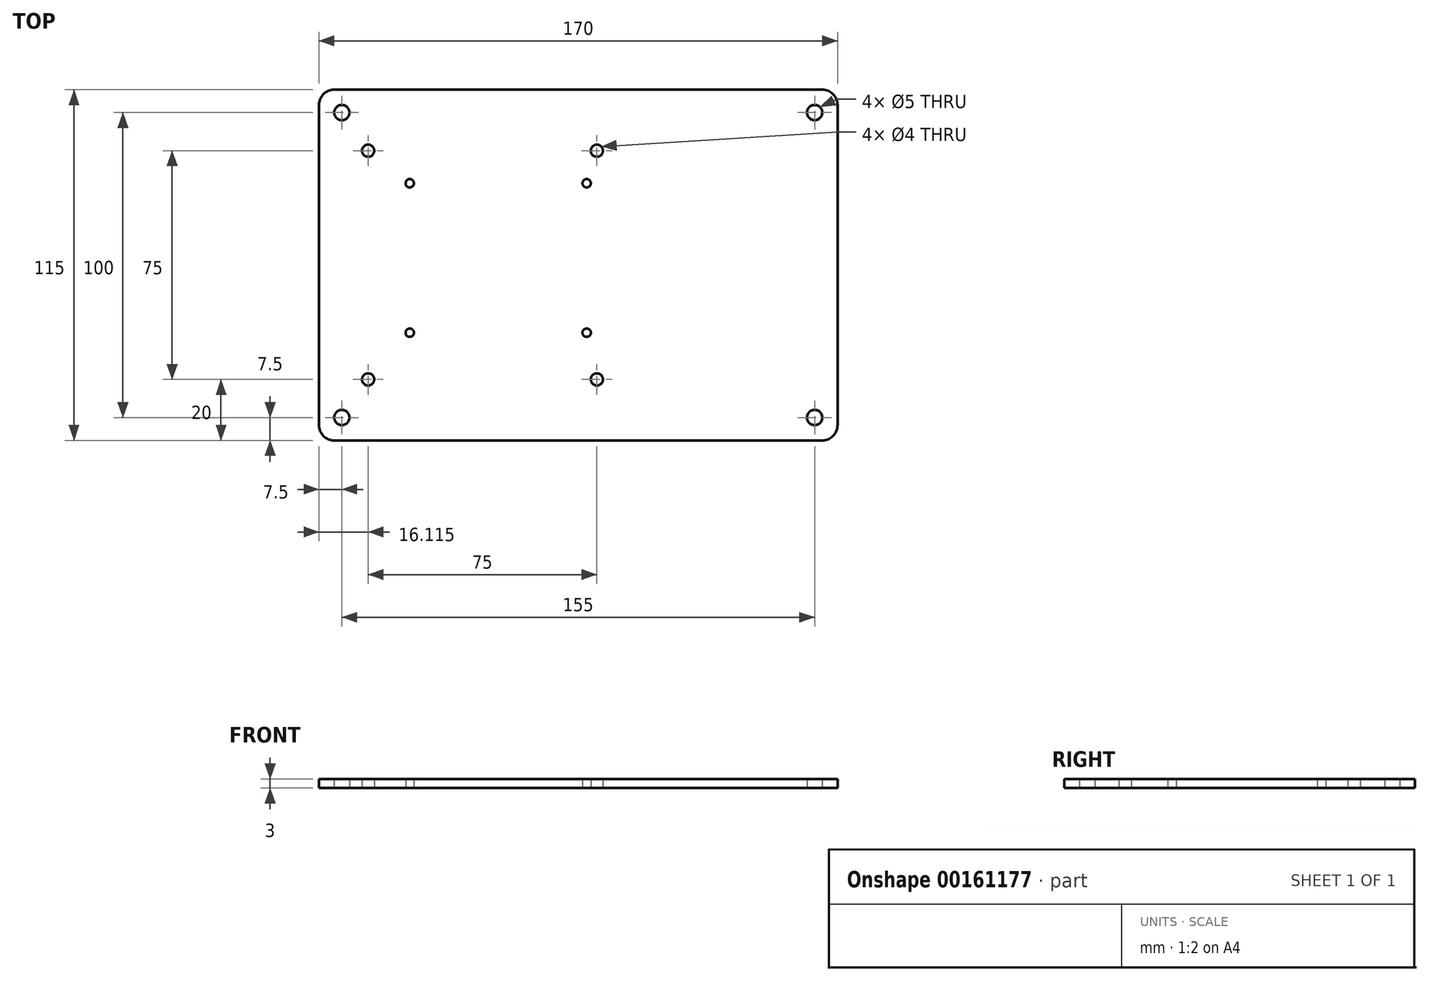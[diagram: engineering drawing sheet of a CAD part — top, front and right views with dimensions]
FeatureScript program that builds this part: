
annotation { "Feature Type Name" : "Feature", "Feature Type Description" : "" }
export const myFeature = defineFeature(function(context is Context, id is Id, definition is map)
    precondition{}
    {
        {
            var Q0;
            Q0=qCreatedBy(makeId("Top.planeOp"),FACE);
            var sketch = newSketch(context, id + "F0", { "sketchPlane" : qUnion([Q0])});
            skLineSegment(sketch, "E0.bottom", {"start": v(-85, 57.5) * mm, "end": v(85, 57.5) * mm});
            skLineSegment(sketch, "E0.top", {"start": v(-85, -57.5) * mm, "end": v(85, -57.5) * mm});
            skLineSegment(sketch, "E0.left", {"start": v(-85, 57.5) * mm, "end": v(-85, -57.5) * mm});
            skLineSegment(sketch, "E0.right", {"start": v(85, 57.5) * mm, "end": v(85, -57.5) * mm});
            skCircle(sketch, "E1", {"center": v(-77.5, 50) * mm, "radius": 2.5 * mm});
            skCircle(sketch, "E2.MirrorC", {"center": v(77.5, 50) * mm, "radius": 2.5 * mm});
            skCircle(sketch, "E3.MirrorC", {"center": v(-77.5, -50) * mm, "radius": 2.5 * mm});
            skCircle(sketch, "E4.MirrorC", {"center": v(77.5, -50) * mm, "radius": 2.5 * mm});
            skCircle(sketch, "E5", {"center": v(-55.23, 26.82) * mm, "radius": 1.38 * mm});
            skCircle(sketch, "E6", {"center": v(2.77, 26.82) * mm, "radius": 1.38 * mm});
            skCircle(sketch, "E7", {"center": v(-55.23, -22.18) * mm, "radius": 1.38 * mm});
            skCircle(sketch, "E8", {"center": v(2.77, -22.18) * mm, "radius": 1.38 * mm});
            skCircle(sketch, "E9", {"center": v(-68.89, 37.5) * mm, "radius": 2 * mm});
            skCircle(sketch, "E10", {"center": v(6.11, 37.5) * mm, "radius": 2 * mm});
            skCircle(sketch, "E11", {"center": v(-68.89, -37.5) * mm, "radius": 2 * mm});
            skCircle(sketch, "E12", {"center": v(6.11, -37.5) * mm, "radius": 2 * mm});
            skSolve(sketch);
        }
        {
            var Q0;
            Q0 = qSketchRegion(id + "F0", true);
            extrude(context, id + "F1", {"entities" : qUnion([Q0]), "depth" : 3 * mm});
        }
        {
            var Q0;
            Q0=makeQuery(id+"F1.opExtrude","SWEPT_EDGE",EDGE,{"disambiguationData":[OSD([sQuery(id+"F0.wireOp",EDGE,"E0.bottom"),sQuery(id+"F0.wireOp",EDGE,"E0.left")])]});
            var Q1;
            Q1=makeQuery(id+"F1.opExtrude","SWEPT_EDGE",EDGE,{"disambiguationData":[OSD([sQuery(id+"F0.wireOp",EDGE,"E0.top"),sQuery(id+"F0.wireOp",EDGE,"E0.right")])]});
            var Q2;
            Q2=makeQuery(id+"F1.opExtrude","SWEPT_EDGE",EDGE,{"disambiguationData":[OSD([sQuery(id+"F0.wireOp",EDGE,"E0.bottom"),sQuery(id+"F0.wireOp",EDGE,"E0.right")])]});
            var Q3;
            Q3=makeQuery(id+"F1.opExtrude","SWEPT_EDGE",EDGE,{"disambiguationData":[OSD([sQuery(id+"F0.wireOp",EDGE,"E0.top"),sQuery(id+"F0.wireOp",EDGE,"E0.left")])]});
            fillet(context, id + "F2", {"entities" : qUnion([Q0, Q1, Q2, Q3]), "radius" : 5 * mm, "allowEdgeOverflow" : false});
        }
    });
